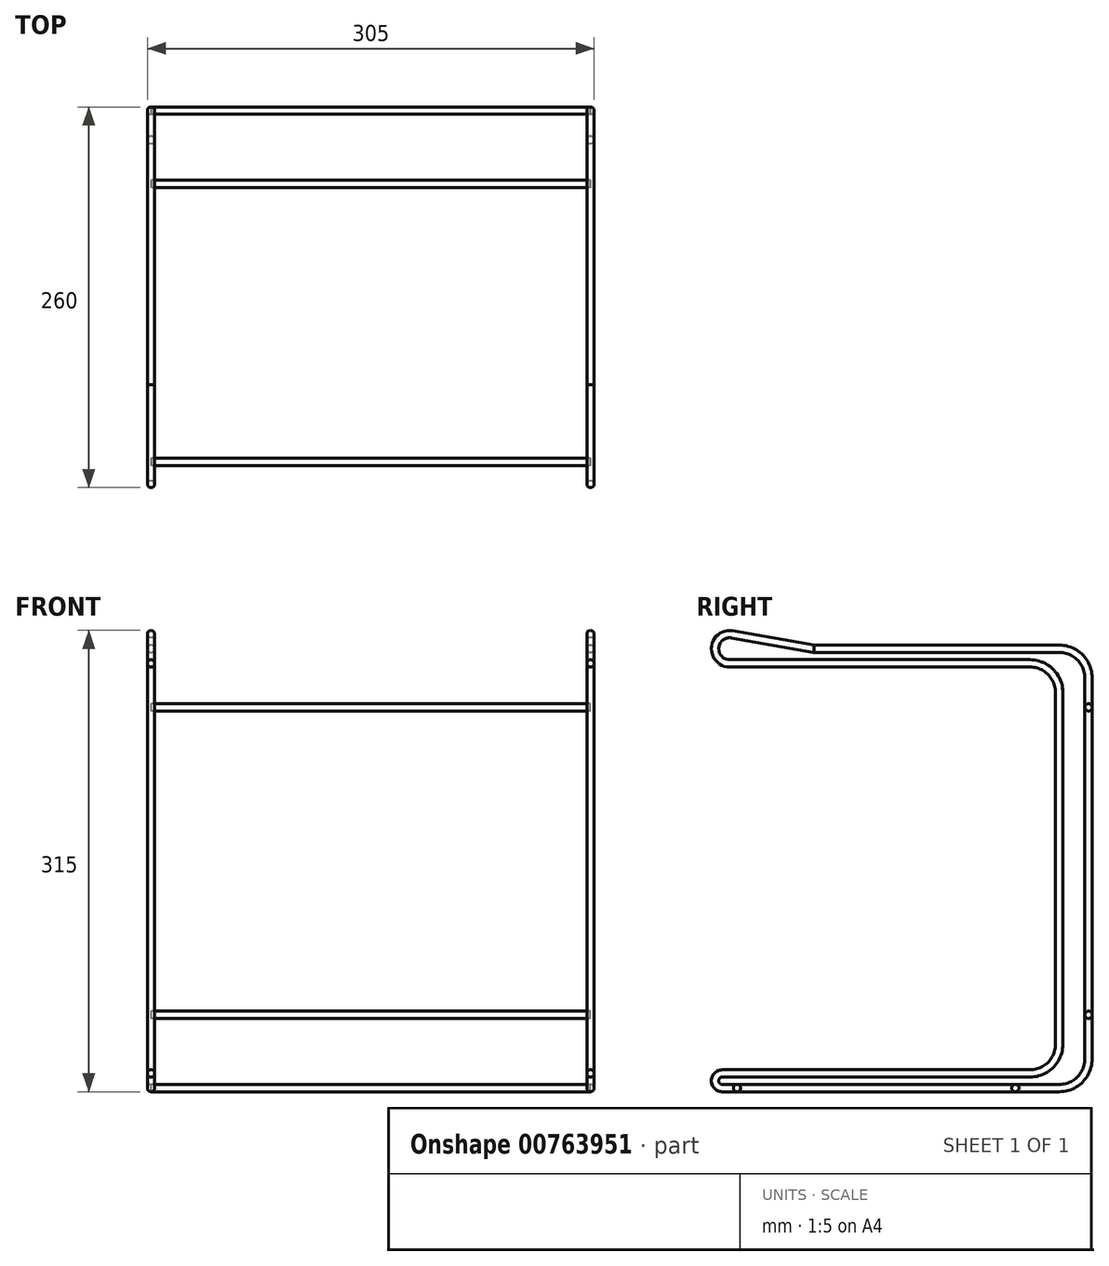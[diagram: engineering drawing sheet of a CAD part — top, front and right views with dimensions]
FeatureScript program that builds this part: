
annotation { "Feature Type Name" : "Feature", "Feature Type Description" : "" }
export const myFeature = defineFeature(function(context is Context, id is Id, definition is map)
    precondition{}
    {
        {
            var Q0;
            Q0=qCreatedBy(makeId("Right.planeOp"),FACE);
            var sketch = newSketch(context, id + "F0", { "sketchPlane" : qUnion([Q0])});
            skLineSegment(sketch, "E0", {"start": v(0, 20) * mm, "end": v(0, 280) * mm});
            skLineSegment(sketch, "E1", {"start": v(-20, 300) * mm, "end": v(-187.41, 300) * mm});
            skLineSegment(sketch, "E2", {"start": v(-245, 290) * mm, "end": v(-40, 290) * mm});
            skLineSegment(sketch, "E3", {"start": v(-20, 270) * mm, "end": v(-20, 30) * mm});
            skLineSegment(sketch, "E4", {"start": v(-40, 10) * mm, "end": v(-250, 10) * mm});
            skLineSegment(sketch, "E5", {"start": v(-255, 5) * mm, "end": v(-255, 5) * mm});
            skLineSegment(sketch, "E6", {"start": v(-250, 0) * mm, "end": v(-20, 0) * mm});
            skArc(sketch, "E7", {"start": v(-243.26, 309.85) * mm, "mid": v(-254.96, 300.87) * mm, "end": v(-245, 290) * mm});
            skLineSegment(sketch, "E8", {"start": v(-243.26, 309.85) * mm, "end": v(-187.41, 300) * mm});
            skPoint(sketch, "E9.visualSharp", {"position": v(-255, 10) * mm});
            skPoint(sketch, "E10.visualSharp", {"position": v(-255, 0) * mm});
            skPoint(sketch, "E11.visualSharp", {"position": v(-20, 290) * mm});
            skArc(sketch, "E11.filletArc", {"start": v(-20, 270) * mm, "mid": v(-25.86, 284.14) * mm, "end": v(-40, 290) * mm});
            skPoint(sketch, "E12.visualSharp", {"position": v(-20, 10) * mm});
            skArc(sketch, "E12.filletArc", {"start": v(-40, 10) * mm, "mid": v(-25.86, 15.86) * mm, "end": v(-20, 30) * mm});
            skPoint(sketch, "E13.visualSharp", {"position": v(0, 300) * mm});
            skArc(sketch, "E13.filletArc", {"start": v(0, 280) * mm, "mid": v(-5.86, 294.14) * mm, "end": v(-20, 300) * mm});
            skPoint(sketch, "E14.visualSharp", {"position": v(0, 0) * mm});
            skArc(sketch, "E14.filletArc", {"start": v(-20, 0) * mm, "mid": v(-5.86, 5.86) * mm, "end": v(0, 20) * mm});
            skArc(sketch, "E15", {"start": v(-250, 10) * mm, "mid": v(-255, 5) * mm, "end": v(-250, 0) * mm});
            skLineSegment(sketch, "E16", {"start": v(-255, 10) * mm, "end": v(-255, 0) * mm});
            skSolve(sketch);
        }
        {
            var Q0;
            Q0=qCreatedBy(makeId("Top.planeOp"),FACE);
            cPlane(context, id + "F1", {"entities" : qUnion([Q0]), "cplaneType" : CPlaneType.OFFSET, "offset" : 25 * mm, "width" : 150 * mm, "height" : 150 * mm});
        }
        {
            var Q0;
            Q0=qCreatedBy(id+"F1.planeOp",FACE);
            var sketch = newSketch(context, id + "F2", { "sketchPlane" : qUnion([Q0])});
            skCircle(sketch, "E17", {"center": v(0, 0) * mm, "radius": 2.5 * mm});
            skSolve(sketch);
        }
        {
            var Q0;
            Q0=makeQuery(id+"F2.imprint","IMPRINT",FACE,{"disambiguationData":[TD([[makeQuery(id+"F2.imprint","IMPRINT",EDGE,{"derivedFrom":sQuery(id+"F2.wireOp",EDGE,"E17")}),1.0]])]});
            var Q1;
            Q1=sQuery(id+"F0.wireOp",EDGE,"E0");
            var Q2;
            Q2=sQuery(id+"F0.wireOp",EDGE,"E14.filletArc");
            var Q3;
            Q3=sQuery(id+"F0.wireOp",EDGE,"E6");
            var Q4;
            Q4=sQuery(id+"F0.wireOp",EDGE,"E12.filletArc");
            var Q5;
            Q5=sQuery(id+"F0.wireOp",EDGE,"E4");
            var Q6;
            Q6=sQuery(id+"F0.wireOp",EDGE,"E13.filletArc");
            var Q7;
            Q7=sQuery(id+"F0.wireOp",EDGE,"E1");
            var Q8;
            Q8=sQuery(id+"F0.wireOp",EDGE,"E8");
            var Q9;
            Q9=sQuery(id+"F0.wireOp",EDGE,"E7");
            var Q10;
            Q10=sQuery(id+"F0.wireOp",EDGE,"E2");
            var Q11;
            Q11=sQuery(id+"F0.wireOp",EDGE,"E11.filletArc");
            var Q12;
            Q12=sQuery(id+"F0.wireOp",EDGE,"E3");
            var Q13;
            Q13=sQuery(id+"F0.wireOp",EDGE,"E9.filletArc");
            var Q14;
            Q14=sQuery(id+"F0.wireOp",EDGE,"E15");
            sweep(context, id + "F3", {"profiles" : qUnion([Q0]), "path" : qUnion([Q1, Q2, Q3, Q4, Q5, Q6, Q7, Q8, Q9, Q10, Q11, Q12, Q13, Q14])});
        }
        {
            var Q0;
            Q0=qCreatedBy(makeId("Right.planeOp"),FACE);
            cPlane(context, id + "F4", {"entities" : qUnion([Q0]), "cplaneType" : CPlaneType.OFFSET, "offset" : 150 * mm, "width" : 150 * mm, "height" : 150 * mm});
        }
        {
            var Q0;
            Q0=makeQuery(id+"F3.opSweep","SWEPT_BODY",BODY,{"disambiguationData":[OSD([sQuery(id+"F0.wireOp",EDGE,"E14.filletArc"),sQuery(id+"F2.wireOp",EDGE,"E17")])]});
            var Q1;
            Q1=qCreatedBy(id+"F4.planeOp",FACE);
            mirror(context, id + "F5", {"entities" : qUnion([Q0]), "mirrorPlane" : qUnion([Q1])});
        }
        {
            var Q0;
            Q0=qCreatedBy(makeId("Front.planeOp"),FACE);
            var sketch = newSketch(context, id + "F6", { "sketchPlane" : qUnion([Q0])});
            skLineSegment(sketch, "E18", {"start": v(0, 50) * mm, "end": v(300, 50) * mm});
            skLineSegment(sketch, "E19", {"start": v(0, 260) * mm, "end": v(300, 260) * mm});
            skSolve(sketch);
        }
        {
            var Q0;
            Q0=qCreatedBy(makeId("Right.planeOp"),FACE);
            var sketch = newSketch(context, id + "F7", { "sketchPlane" : qUnion([Q0])});
            skCircle(sketch, "E20", {"center": v(0, 260) * mm, "radius": 2.5 * mm});
            skCircle(sketch, "E21", {"center": v(0, 50) * mm, "radius": 2.5 * mm});
            skCircle(sketch, "E22", {"center": v(-50, 0) * mm, "radius": 2.5 * mm});
            skCircle(sketch, "E23", {"center": v(-240, 0) * mm, "radius": 2.5 * mm});
            skSolve(sketch);
        }
        {
            var Q0;
            Q0 = qSketchRegion(id + "F7", true);
            extrude(context, id + "F8", {"entities" : qUnion([Q0]), "depth" : 300 * mm, "offsetDistance" : 25 * mm});
        }
    });
